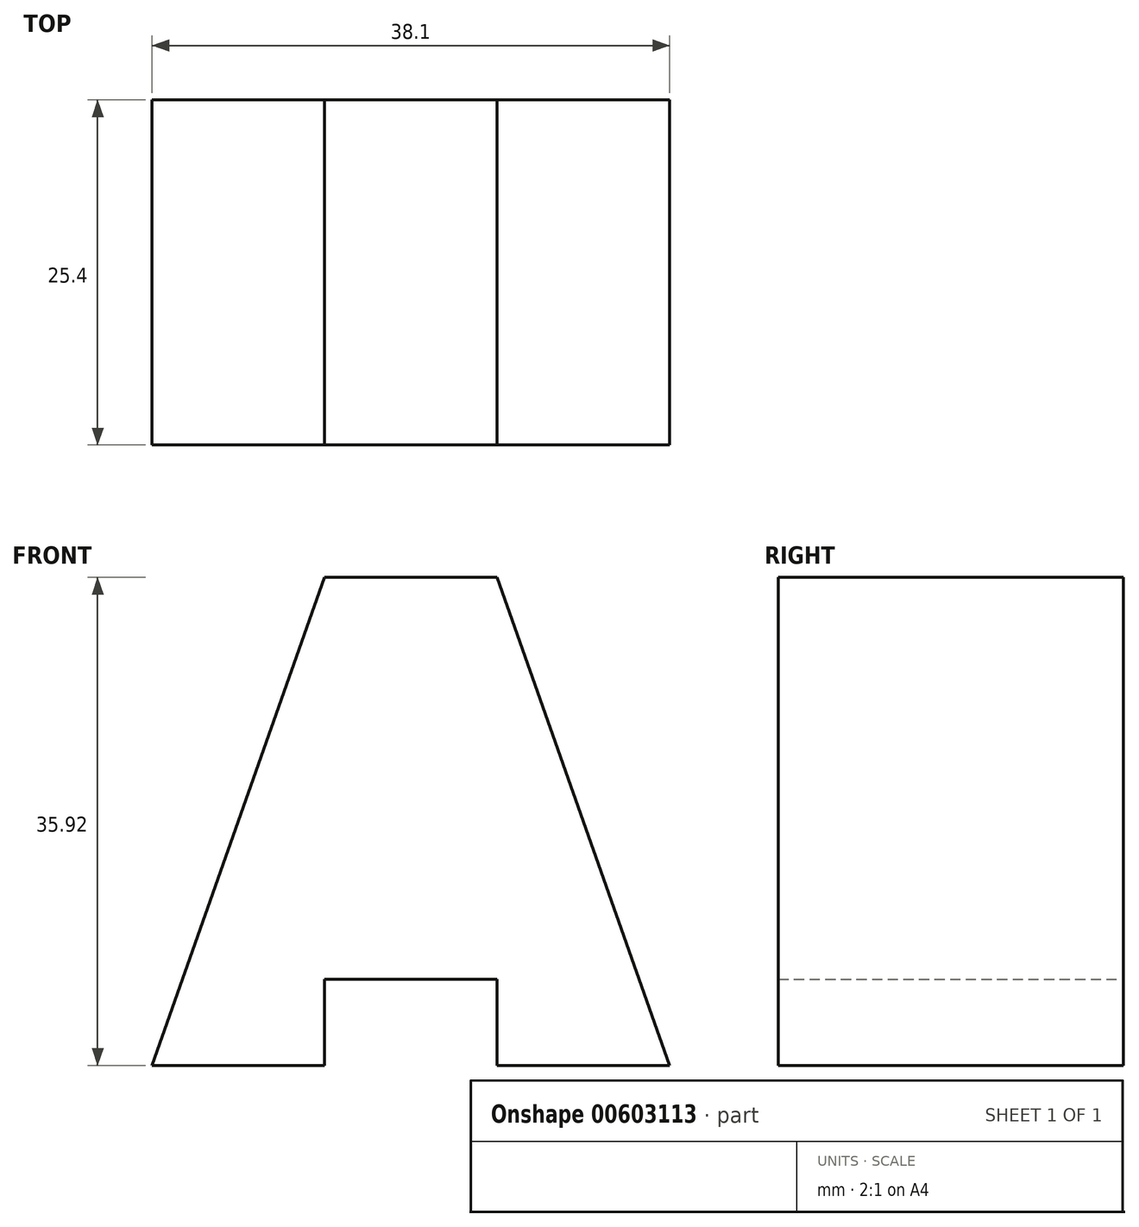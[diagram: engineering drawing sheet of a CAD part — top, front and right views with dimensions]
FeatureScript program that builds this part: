
annotation { "Feature Type Name" : "Feature", "Feature Type Description" : "" }
export const myFeature = defineFeature(function(context is Context, id is Id, definition is map)
    precondition{}
    {
        {
            var Q0;
            Q0=qCreatedBy(makeId("Front.planeOp"),FACE);
            var sketch = newSketch(context, id + "F0", { "sketchPlane" : qUnion([Q0])});
            skLineSegment(sketch, "E0", {"start": v(0, 0) * mm, "end": v(12.7, 0) * mm});
            skLineSegment(sketch, "E1", {"start": v(12.7, 0) * mm, "end": v(12.7, 6.35) * mm});
            skLineSegment(sketch, "E2", {"start": v(12.7, 6.35) * mm, "end": v(25.4, 6.35) * mm});
            skLineSegment(sketch, "E3", {"start": v(25.4, 6.35) * mm, "end": v(25.4, 0) * mm});
            skLineSegment(sketch, "E4", {"start": v(25.4, 0) * mm, "end": v(38.1, 0) * mm});
            skLineSegment(sketch, "E5", {"start": v(38.1, 0) * mm, "end": v(25.4, 35.92) * mm});
            skLineSegment(sketch, "E6", {"start": v(25.4, 35.92) * mm, "end": v(12.7, 35.92) * mm});
            skLineSegment(sketch, "E7", {"start": v(12.7, 35.92) * mm, "end": v(0, 0) * mm});
            skSolve(sketch);
        }
        {
            var Q0;
            Q0 = qSketchRegion(id + "F0", true);
            extrude(context, id + "F1", {"entities" : qUnion([Q0]), "depth" : 25.4 * mm, "offsetDistance" : 25.4 * mm});
        }
    });
